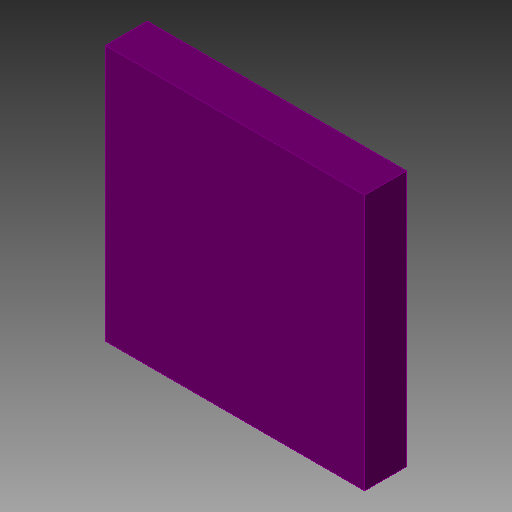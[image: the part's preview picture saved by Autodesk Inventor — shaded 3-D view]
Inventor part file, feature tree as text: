
AUTODESK INVENTOR PART (.ipt)
format: ipt  version: 2018 (Build 220112000, 112)  size: 80,896 bytes
history: native  units: in
note: dims shown in document units (in); Inventor stores cm internally (conversion verified against a paired STEP export)
features: other x1, extrude x1
ambient origin geometry x8: Origin, YZ Plane, XZ Plane, XY Plane, X Axis, Y Axis, Z Axis, Center Point
bodies: Solid1 (feature_tree)
feature tree (2):
  other  "PBTH, S2_PBTH_140"
  extrude  "Extrusion1"  Depth=0.0394in TaperAngle=0.0deg
